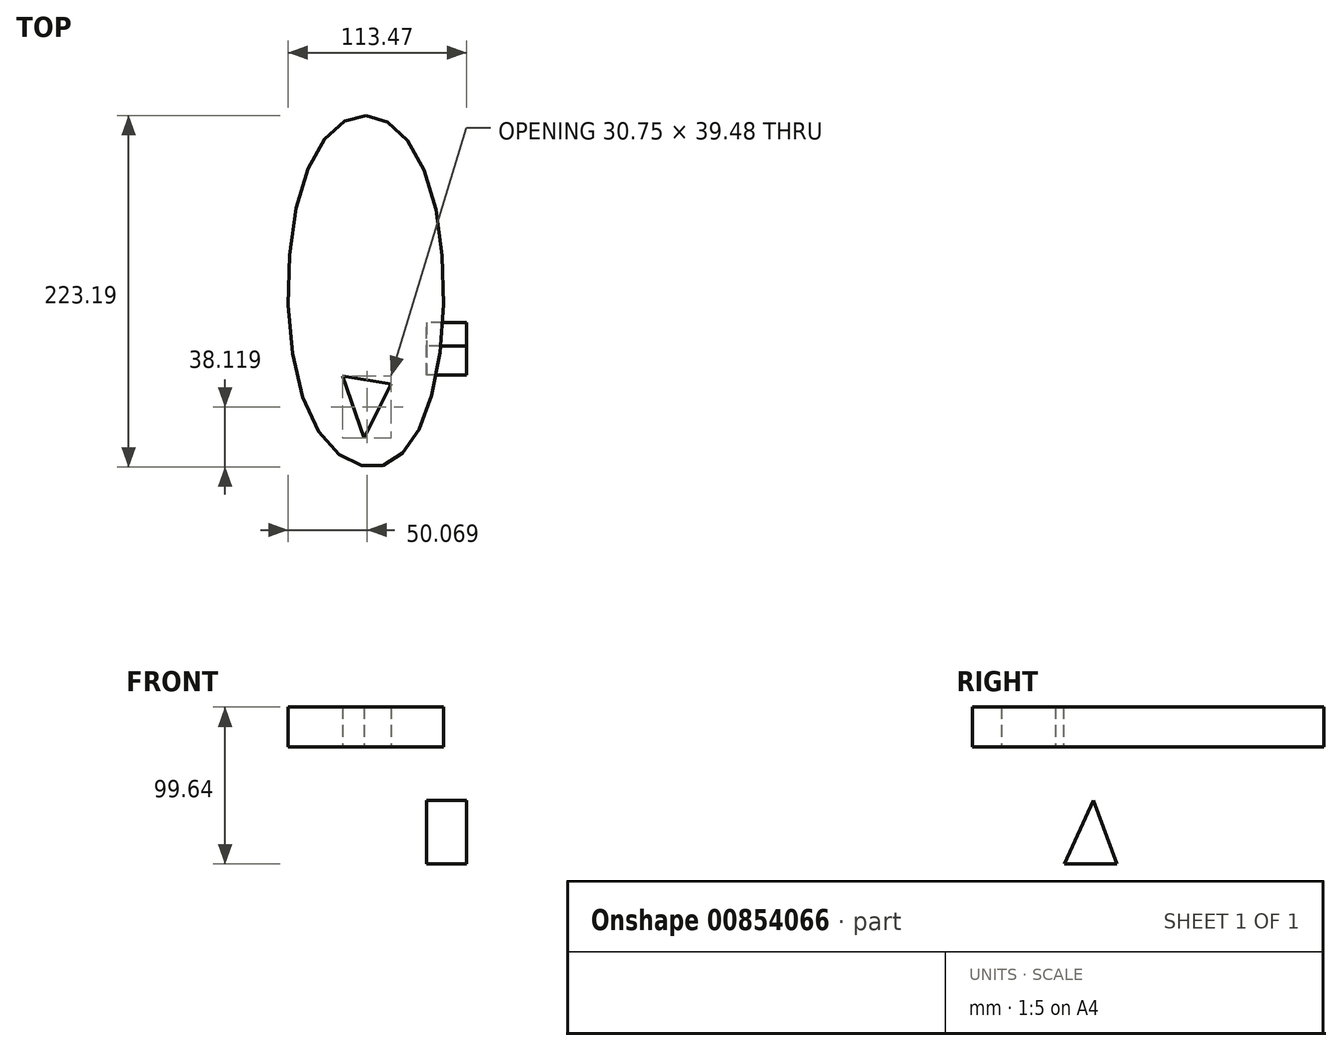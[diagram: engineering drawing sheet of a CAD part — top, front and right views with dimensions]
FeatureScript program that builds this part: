
annotation { "Feature Type Name" : "Feature", "Feature Type Description" : "" }
export const myFeature = defineFeature(function(context is Context, id is Id, definition is map)
    precondition{}
    {
        {
            var Q0;
            Q0=qCreatedBy(makeId("Top.planeOp"),FACE);
            var sketch = newSketch(context, id + "F0", { "sketchPlane" : qUnion([Q0])});
            skFitSpline(sketch, "E0", {"points": [v(-38.65, 112.62) * mm, v(0, 73.97) * mm, v(0, -75.27) * mm, v(-33.45, -110.52) * mm, v(-75.1, -76.06) * mm, v(-76.25, 77) * mm, v(-38.65, 112.62) * mm]});
            skLineSegment(sketch, "E1", {"start": v(-53.37, -52.7) * mm, "end": v(-39.76, -92.2) * mm});
            skLineSegment(sketch, "E2", {"start": v(-39.76, -92.2) * mm, "end": v(-22.63, -57.77) * mm});
            skLineSegment(sketch, "E3", {"start": v(-22.63, -57.77) * mm, "end": v(-53.37, -52.7) * mm});
            skSolve(sketch);
        }
        {
            var Q0;
            Q0=makeQuery(id+"F0.imprint","IMPRINT",FACE,{"disambiguationData":[TD([[makeQuery(id+"F0.imprint","IMPRINT",EDGE,{"derivedFrom":sQuery(id+"F0.wireOp",EDGE,"E0")}),-1.0]])]});
            extrude(context, id + "F1", {"entities" : qUnion([Q0]), "depth" : 25.4 * mm, "offsetDistance" : 25.4 * mm});
        }
        {
            var Q0;
            Q0=qCreatedBy(makeId("Right.planeOp"),FACE);
            var sketch = newSketch(context, id + "F2", { "sketchPlane" : qUnion([Q0])});
            skLineSegment(sketch, "E4", {"start": v(-33.67, -34) * mm, "end": v(-52.11, -74.24) * mm});
            skLineSegment(sketch, "E5", {"start": v(-52.11, -74.24) * mm, "end": v(-18.85, -74.24) * mm});
            skLineSegment(sketch, "E6", {"start": v(-18.85, -74.24) * mm, "end": v(-33.67, -34) * mm});
            skSolve(sketch);
        }
        {
            var Q0;
            Q0=makeQuery(id+"F2.imprint","IMPRINT",FACE,{"disambiguationData":[TD([[makeQuery(id+"F2.imprint","IMPRINT",EDGE,{"derivedFrom":sQuery(id+"F2.wireOp",EDGE,"E4")}),1.0]])]});
            extrude(context, id + "F3", {"entities" : qUnion([Q0]), "depth" : 25.4 * mm, "offsetDistance" : 25.4 * mm});
        }
    });
